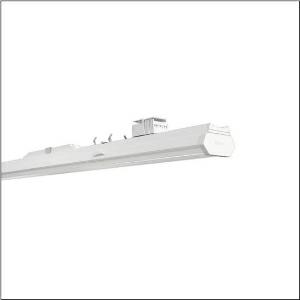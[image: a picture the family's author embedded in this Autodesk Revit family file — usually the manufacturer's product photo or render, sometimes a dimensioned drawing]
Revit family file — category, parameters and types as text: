
# Revit family: licross_r__21_protected_mo_52tp117n485g_3f7e
name_source: partatom
category: Lighting Fixtures
units: mm (PartAtom-declared; Revit-internal decimal feet)

## family parameters
Cut with Voids When Loaded = No
Host = Face
Light Source = No
Part Type = Normal
Room Calculation Point = No
Round Connector Dimension = Use Diameter
Shared = No

## types (1)
- Licross® 21 Protected MO (1 x LED, 8570 lm, 47.9 W, 4000K)
    Apparent Load = 48 VA
    CIE Flux Codes = 83 94 98 100 100
    Color Rendering = 80
    Color Temperature = 4000K
    Default Elevation = 1800 mm
    Description = Licross® 21 Protected MO, luminaire insert, of sheet steel, galvanised, coil coated, white, length: 1.500mm, width: 66mm, height: 67mm, LED rated luminous flux: 8.570lm, light colour: 840, control gear: ON/OFF, with plug, 3-pole, with phase selection, mains connection: 220..240V, AC, 50/60Hz, rated input power: 48W, internal wiring halogen-free, primary light control with lens, of plastic, primary optical cover: cover, of PMMA, light emission: direct distribution, primary light characteristic: symmetric, protection rating (complete): IP64, insulation class (complete): insulation class I (protective earthing), certification: CE, ENEC, VDE, UKCA, protection symbol: D if used in an environment with conductive dust loads with corresponding accessories, impact resistance: IK06, permissible ambient temperature for indoor applications: -35..+45°C, corresponds to IFS (International Featured Standards) requirements for safety and quality in the food industry, reducing of maximum allowable ambient temperature of 5°C with ceiling mounting, LABS conformity tested according to VDMA 24364:2018-05, packaging unit: 1 piece
    Height = 92 mm
    Lamp = 1 x LED
    Lamp Light Flux = 8570 lm
    Lamp Power = 47.9 W
    Lamp count = 1
    Length = 1500 mm
    Luminous efficacy = 179 lm/W
    Manufacturer = Siteco
    ModVariant = No
    Model = 52TP117N485G
    Mounting Place = Ceiling
    Mounting Type = Pendant
    Number of Poles = 1
    OnlyDefault = Yes
    Power Factor = 1
    Product Name = Licross® 21 Protected MO
    Product group = luminaire insert | ceiling pendant
    ProductGroupID = 902
    Protection Class = Protection class I
    Protection Degree = IP 64
    RLX_Detail_Level = 1
    RLX_Emergency_Light_Flux = 0 lm
    RLX_Emergency_Type = 0
    RLX_Emergency_Type_DB = No
    RlxData = <blob elided: 20517 chars, md5=3bb2d163>
    Socket = socket
    Standby Power = 0 W
    System Light Flux = 8570 lm
    System Power = 48 W
    Type Comments = Product without accessories
    Type Image = l_1256148.jpg
    URL = http://relux.com
    VarID = ---
    Voltage = 0 V
    Weight = 0.00 kg
    Width = 88 mm

## geometry (parser evidence)
native form markers: Blend x4, Sweep x11
no freeform markers — native parametric forms only
